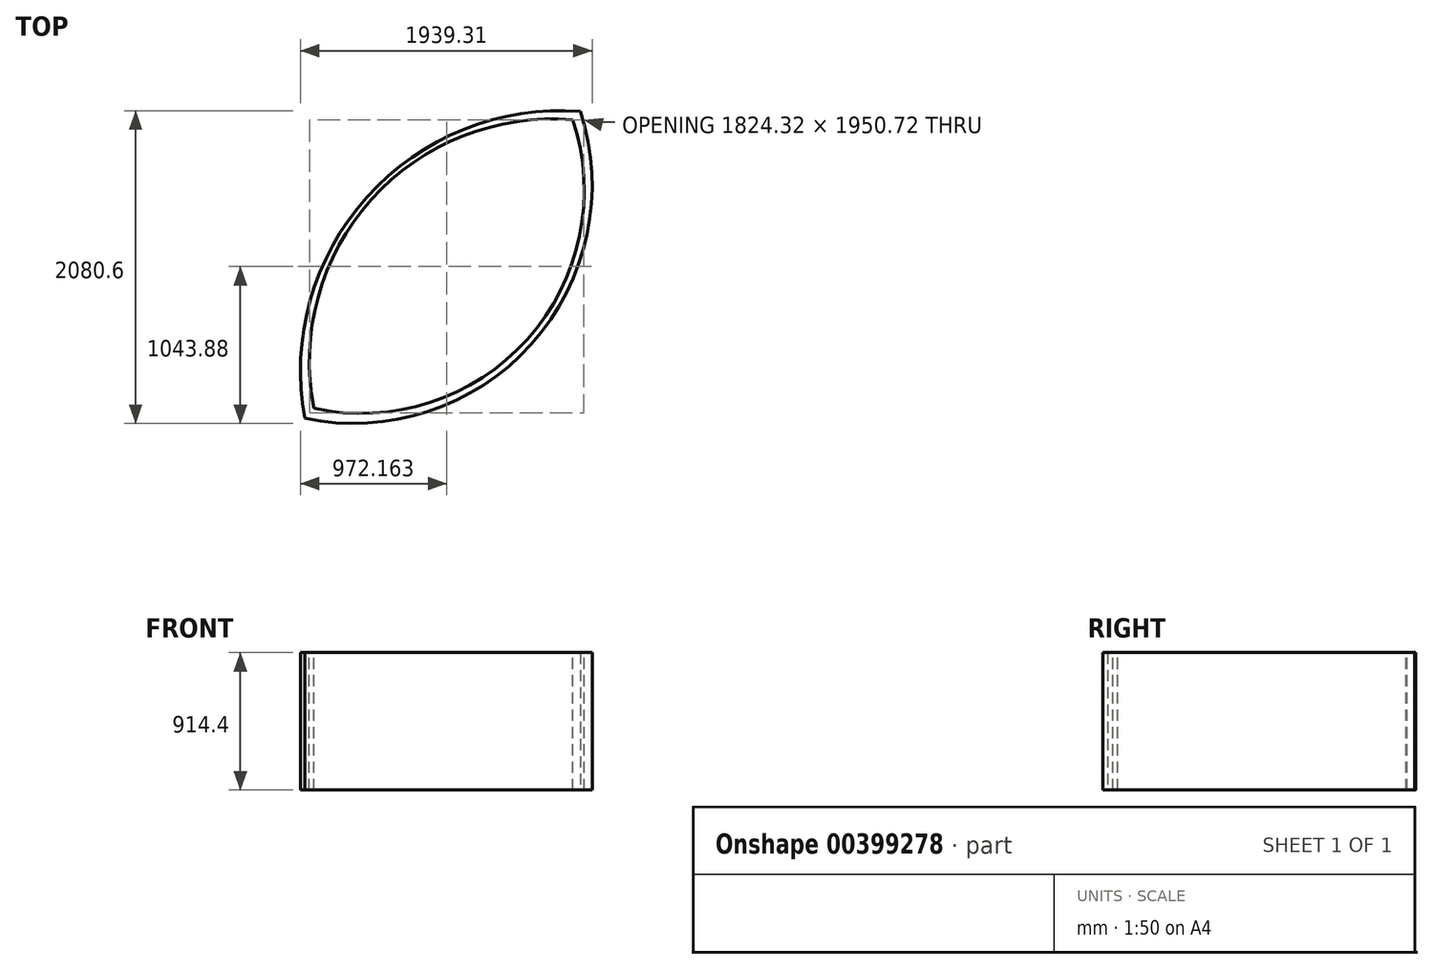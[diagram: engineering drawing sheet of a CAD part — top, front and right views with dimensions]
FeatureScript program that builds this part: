
annotation { "Feature Type Name" : "Feature", "Feature Type Description" : "" }
export const myFeature = defineFeature(function(context is Context, id is Id, definition is map)
    precondition{}
    {
        {
            var Q0;
            Q0=qCreatedBy(makeId("Top.planeOp"),FACE);
            var sketch = newSketch(context, id + "F0", { "sketchPlane" : qUnion([Q0])});
            skArc(sketch, "E0", {"start": v(728.13, 1317.26) * mm, "mid": v(-690.73, 747.56) * mm, "end": v(-1103.88, -724.52) * mm});
            skArc(sketch, "E1", {"start": v(-1103.88, -724.52) * mm, "mid": v(401.1, -232.09) * mm, "end": v(728.13, 1317.26) * mm});
            skSolve(sketch);
        }
        {
            var Q0;
            Q0=makeQuery(id+"F0.imprint","IMPRINT",FACE,{"disambiguationData":[TD([[makeQuery(id+"F0.imprint","IMPRINT",EDGE,{"derivedFrom":sQuery(id+"F0.wireOp",EDGE,"E0")}),1.0]])]});
            var Q1;
            Q1=sQuery(id+"F0.wireOp",EDGE,"E0");
            var Q2;
            Q2=sQuery(id+"F0.wireOp",EDGE,"E1");
            extrude(context, id + "F1", {"entities" : qUnion([Q0]), "surfaceEntities" : qUnion([Q1, Q2]), "depth" : 914.4 * mm});
        }
        {
            var Q0;
            Q0=makeQuery(id+"F1.opExtrude","CAP_FACE",FACE,{"disambiguationData":[OSD([sQuery(id+"F0.wireOp",EDGE,"E0"),sQuery(id+"F0.wireOp",EDGE,"E1")])],"isStart":false});
            var sketch = newSketch(context, id + "F2", { "sketchPlane" : qUnion([Q0])});
            skLineSegment(sketch, "E2", {"start": v(-1103.88, -724.52) * mm, "end": v(728.13, 1317.26) * mm, "construction": true});
            skArc(sketch, "E3", {"start": v(-1044.1, -657.9) * mm, "mid": v(374.54, -199.01) * mm, "end": v(677.55, 1260.88) * mm});
            skArc(sketch, "E4", {"start": v(677.55, 1260.88) * mm, "mid": v(-661.51, 730.6) * mm, "end": v(-1044.1, -657.9) * mm});
            skSolve(sketch);
        }
        {
            var Q0;
            Q0=makeQuery(id+"F2.imprint","IMPRINT",FACE,{"disambiguationData":[TD([[makeQuery(id+"F2.imprint","IMPRINT",EDGE,{"derivedFrom":sQuery(id+"F2.wireOp",EDGE,"E3")}),1.0]])]});
            var Q1;
            Q1=sQuery(id+"F2.wireOp",EDGE,"E4");
            var Q2;
            Q2=sQuery(id+"F2.wireOp",EDGE,"E3");
            extrude(context, id + "F3", {"entities" : qUnion([Q0]), "operationType" : NewBodyOperationType.REMOVE, "surfaceEntities" : qUnion([Q1, Q2]), "endBound" : BoundingType.THROUGH_ALL, "oppositeDirection" : true, "depth" : 25.4 * mm});
        }
    });
